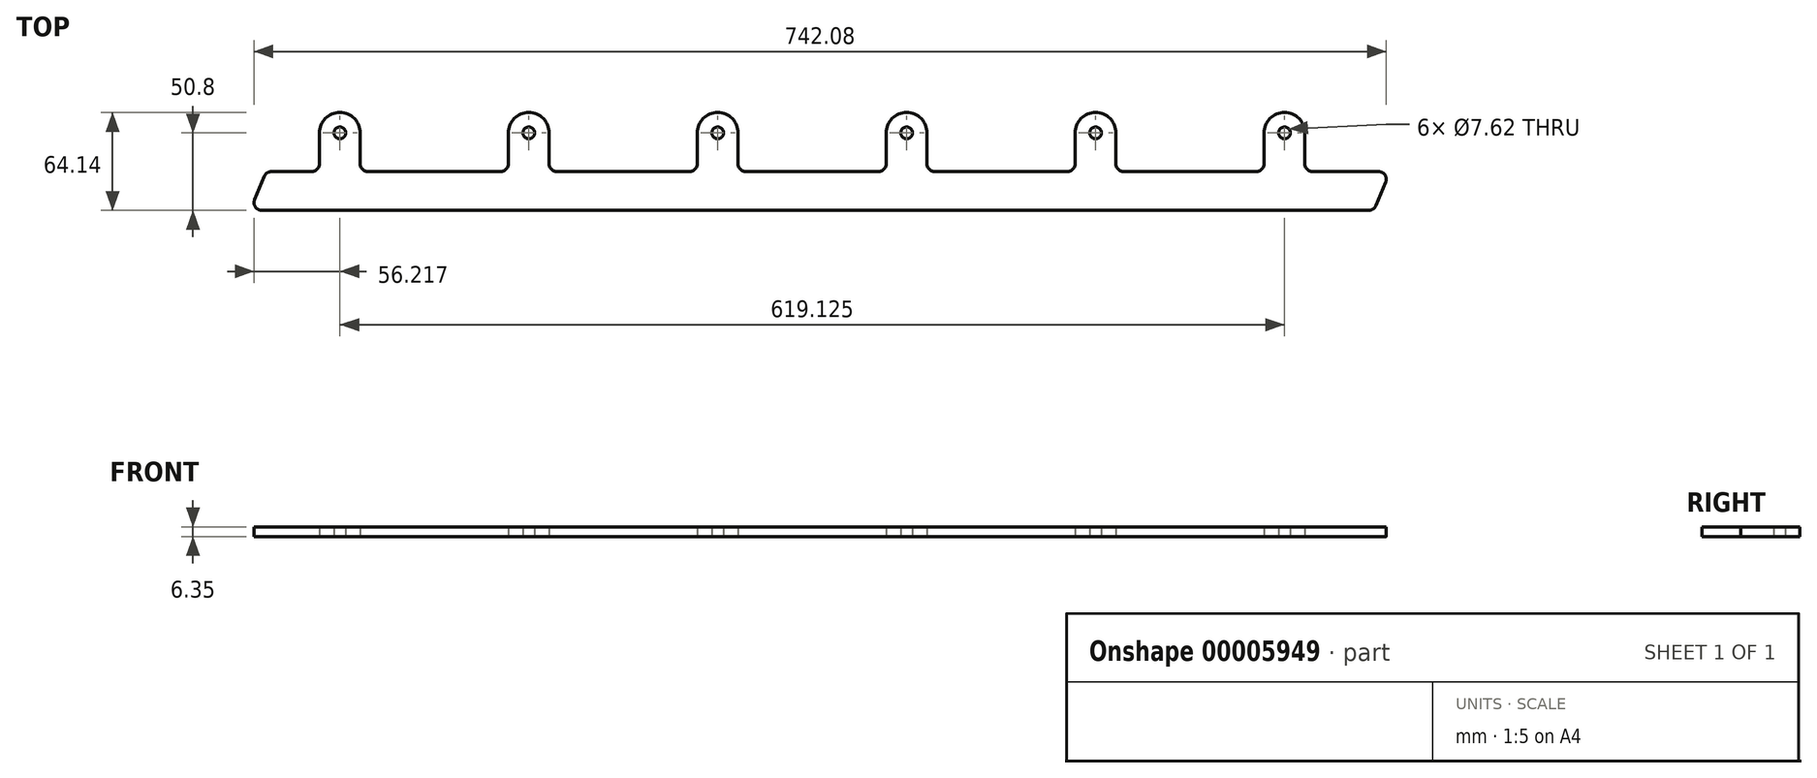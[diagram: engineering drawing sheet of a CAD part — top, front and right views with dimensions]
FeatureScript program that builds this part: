
annotation { "Feature Type Name" : "Feature", "Feature Type Description" : "" }
export const myFeature = defineFeature(function(context is Context, id is Id, definition is map)
    precondition{}
    {
        {
            var Q0;
            Q0=qCreatedBy(makeId("Top.planeOp"),FACE);
            var sketch = newSketch(context, id + "F0", { "sketchPlane" : qUnion([Q0])});
            skLineSegment(sketch, "E0.rect.bottom", {"start": v(368.3, 12.7) * mm, "end": v(-296.23, 12.7) * mm});
            skLineSegment(sketch, "E0.rect.top", {"start": v(368.3, -12.7) * mm, "end": v(-368.3, -12.7) * mm});
            skLineSegment(sketch, "E0.rect.left", {"start": v(368.3, 12.7) * mm, "end": v(368.3, -12.7) * mm, "construction": true});
            skLineSegment(sketch, "E0.rect.right", {"start": v(-368.3, 12.7) * mm, "end": v(-368.3, -12.7) * mm, "construction": true});
            skPoint(sketch, "E0.rect.middle", {"position": v(0, 0) * mm});
            skCircle(sketch, "E1", {"center": v(-309.56, 38.1) * mm, "radius": 3.81 * mm});
            skArc(sketch, "E2.0", {"start": v(-296.23, 38.1) * mm, "mid": v(-309.56, 51.44) * mm, "end": v(-322.9, 38.1) * mm});
            skLineSegment(sketch, "E3", {"start": v(-322.9, 38.1) * mm, "end": v(-322.9, 12.7) * mm});
            skLineSegment(sketch, "E4", {"start": v(-296.23, 38.1) * mm, "end": v(-296.23, 12.7) * mm});
            skLineSegment(sketch, "E5.trimOffspring", {"start": v(-322.9, 12.7) * mm, "end": v(-357.78, 12.7) * mm});
            skLineSegment(sketch, "E6.1.0.0", {"start": v(-199.07, 38.1) * mm, "end": v(-199.07, 12.7) * mm});
            skArc(sketch, "E6.1.0.1", {"start": v(-172.4, 38.1) * mm, "mid": v(-185.74, 51.44) * mm, "end": v(-199.07, 38.1) * mm});
            skCircle(sketch, "E6.1.0.2", {"center": v(-185.74, 38.1) * mm, "radius": 3.81 * mm});
            skLineSegment(sketch, "E6.1.0.3", {"start": v(-172.4, 38.1) * mm, "end": v(-172.4, 12.7) * mm});
            skLineSegment(sketch, "E6.2.0.0", {"start": v(-75.25, 38.1) * mm, "end": v(-75.25, 12.7) * mm});
            skArc(sketch, "E6.2.0.1", {"start": v(-48.58, 38.1) * mm, "mid": v(-61.91, 51.44) * mm, "end": v(-75.25, 38.1) * mm});
            skCircle(sketch, "E6.2.0.2", {"center": v(-61.91, 38.1) * mm, "radius": 3.81 * mm});
            skLineSegment(sketch, "E6.2.0.3", {"start": v(-48.58, 38.1) * mm, "end": v(-48.58, 12.7) * mm});
            skLineSegment(sketch, "E6.3.0.0", {"start": v(48.58, 38.1) * mm, "end": v(48.58, 12.7) * mm});
            skArc(sketch, "E6.3.0.1", {"start": v(75.25, 38.1) * mm, "mid": v(61.91, 51.44) * mm, "end": v(48.58, 38.1) * mm});
            skCircle(sketch, "E6.3.0.2", {"center": v(61.91, 38.1) * mm, "radius": 3.81 * mm});
            skLineSegment(sketch, "E6.3.0.3", {"start": v(75.25, 38.1) * mm, "end": v(75.25, 12.7) * mm});
            skLineSegment(sketch, "E6.4.0.0", {"start": v(172.4, 38.1) * mm, "end": v(172.4, 12.7) * mm});
            skArc(sketch, "E6.4.0.1", {"start": v(199.07, 38.1) * mm, "mid": v(185.74, 51.44) * mm, "end": v(172.4, 38.1) * mm});
            skCircle(sketch, "E6.4.0.2", {"center": v(185.74, 38.1) * mm, "radius": 3.81 * mm});
            skLineSegment(sketch, "E6.4.0.3", {"start": v(199.07, 38.1) * mm, "end": v(199.07, 12.7) * mm});
            skLineSegment(sketch, "E6.direction1", {"start": v(-322.9, 12.7) * mm, "end": v(-199.07, 12.7) * mm, "construction": true});
            skLineSegment(sketch, "E7.0.5.0", {"start": v(296.23, 38.1) * mm, "end": v(296.23, 12.7) * mm});
            skArc(sketch, "E7.3.5.0", {"start": v(322.9, 38.1) * mm, "mid": v(309.56, 51.44) * mm, "end": v(296.23, 38.1) * mm});
            skCircle(sketch, "E7.7.5.0", {"center": v(309.56, 38.1) * mm, "radius": 3.81 * mm});
            skLineSegment(sketch, "E7.9.5.0", {"start": v(322.9, 38.1) * mm, "end": v(322.9, 12.7) * mm});
            skLineSegment(sketch, "E8", {"start": v(48.58, 38.1) * mm, "end": v(-48.58, 38.1) * mm, "construction": true});
            skPoint(sketch, "E9", {"position": v(0, 38.1) * mm});
            skLineSegment(sketch, "E10", {"start": v(-368.3, -12.7) * mm, "end": v(-357.78, 12.7) * mm});
            skLineSegment(sketch, "E11", {"start": v(368.3, -12.7) * mm, "end": v(378.82, 12.7) * mm});
            skLineSegment(sketch, "E12", {"start": v(368.3, 12.7) * mm, "end": v(378.82, 12.7) * mm});
            skSolve(sketch);
        }
        {
            var Q0;
            Q0=makeQuery(id+"F0.imprint","IMPRINT",FACE,{"disambiguationData":[TD([[makeQuery(id+"F0.imprint","IMPRINT",EDGE,{"derivedFrom":sQuery(id+"F0.wireOp",EDGE,"E0.rect.top")}),-1.0]])]});
            var Q1;
            {var subQ1=sQuery(id+"F0.wireOp",EDGE,"E6.1.0.0");Q1=makeQuery(id+"F0.imprint","IMPRINT",FACE,{"disambiguationData":[TD([[makeQuery(id+"F0.imprint","IMPRINT",EDGE,{"derivedFrom":subQ1}),1.0]])]});}
            var Q2;
            {var subQ1=sQuery(id+"F0.wireOp",EDGE,"E6.2.0.0");Q2=makeQuery(id+"F0.imprint","IMPRINT",FACE,{"disambiguationData":[TD([[makeQuery(id+"F0.imprint","IMPRINT",EDGE,{"derivedFrom":subQ1}),1.0]])]});}
            var Q3;
            {var subQ1=sQuery(id+"F0.wireOp",EDGE,"E6.3.0.0");Q3=makeQuery(id+"F0.imprint","IMPRINT",FACE,{"disambiguationData":[TD([[makeQuery(id+"F0.imprint","IMPRINT",EDGE,{"derivedFrom":subQ1}),1.0]])]});}
            var Q4;
            {var subQ1=sQuery(id+"F0.wireOp",EDGE,"E6.4.0.0");Q4=makeQuery(id+"F0.imprint","IMPRINT",FACE,{"disambiguationData":[TD([[makeQuery(id+"F0.imprint","IMPRINT",EDGE,{"derivedFrom":subQ1}),1.0]])]});}
            var Q5;
            {var subQ1=sQuery(id+"F0.wireOp",EDGE,"E7.0.5.0");Q5=makeQuery(id+"F0.imprint","IMPRINT",FACE,{"disambiguationData":[TD([[makeQuery(id+"F0.imprint","IMPRINT",EDGE,{"derivedFrom":subQ1}),1.0]])]});}
            extrude(context, id + "F1", {"entities" : qUnion([Q0, Q1, Q2, Q3, Q4, Q5]), "depth" : 6.35 * mm});
        }
        {
            var Q0;
            Q0=makeQuery(id+"F1.opExtrude","SWEPT_EDGE",EDGE,{"disambiguationData":[OSD([sQuery(id+"F0.wireOp",EDGE,"E0.rect.top"),sQuery(id+"F0.wireOp",EDGE,"E11")])]});
            var Q1;
            Q1=makeQuery(id+"F1.opExtrude","SWEPT_EDGE",EDGE,{"disambiguationData":[OSD([sQuery(id+"F0.wireOp",EDGE,"E0.rect.top"),sQuery(id+"F0.wireOp",EDGE,"E10")])]});
            var Q2;
            Q2=makeQuery(id+"F1.opExtrude","SWEPT_EDGE",EDGE,{"disambiguationData":[OSD([sQuery(id+"F0.wireOp",EDGE,"E3"),sQuery(id+"F0.wireOp",EDGE,"E5.trimOffspring")])]});
            var Q3;
            Q3=makeQuery(id+"F1.opExtrude","SWEPT_EDGE",EDGE,{"disambiguationData":[OSD([sQuery(id+"F0.wireOp",EDGE,"E5.trimOffspring"),sQuery(id+"F0.wireOp",EDGE,"E10")])]});
            var Q4;
            Q4=makeQuery(id+"F1.opExtrude","SWEPT_EDGE",EDGE,{"disambiguationData":[OSD([sQuery(id+"F0.wireOp",EDGE,"E0.rect.bottom"),sQuery(id+"F0.wireOp",EDGE,"E6.1.0.0")])]});
            var Q5;
            Q5=makeQuery(id+"F1.opExtrude","SWEPT_EDGE",EDGE,{"disambiguationData":[OSD([sQuery(id+"F0.wireOp",EDGE,"E0.rect.bottom"),sQuery(id+"F0.wireOp",EDGE,"E6.2.0.0")])]});
            var Q6;
            Q6=makeQuery(id+"F1.opExtrude","SWEPT_EDGE",EDGE,{"disambiguationData":[OSD([sQuery(id+"F0.wireOp",EDGE,"E0.rect.bottom"),sQuery(id+"F0.wireOp",EDGE,"E6.3.0.0")])]});
            var Q7;
            Q7=makeQuery(id+"F1.opExtrude","SWEPT_EDGE",EDGE,{"disambiguationData":[OSD([sQuery(id+"F0.wireOp",EDGE,"E0.rect.bottom"),sQuery(id+"F0.wireOp",EDGE,"E6.4.0.0")])]});
            var Q8;
            Q8=makeQuery(id+"F1.opExtrude","SWEPT_EDGE",EDGE,{"disambiguationData":[OSD([sQuery(id+"F0.wireOp",EDGE,"E0.rect.bottom"),sQuery(id+"F0.wireOp",EDGE,"E7.0.5.0")])]});
            var Q9;
            Q9=makeQuery(id+"F1.opExtrude","SWEPT_EDGE",EDGE,{"disambiguationData":[OSD([sQuery(id+"F0.wireOp",EDGE,"E0.rect.bottom"),sQuery(id+"F0.wireOp",EDGE,"E4")])]});
            var Q10;
            Q10=makeQuery(id+"F1.opExtrude","SWEPT_EDGE",EDGE,{"disambiguationData":[OSD([sQuery(id+"F0.wireOp",EDGE,"E0.rect.bottom"),sQuery(id+"F0.wireOp",EDGE,"E6.1.0.3")])]});
            var Q11;
            Q11=makeQuery(id+"F1.opExtrude","SWEPT_EDGE",EDGE,{"disambiguationData":[OSD([sQuery(id+"F0.wireOp",EDGE,"E0.rect.bottom"),sQuery(id+"F0.wireOp",EDGE,"E6.2.0.3")])]});
            var Q12;
            Q12=makeQuery(id+"F1.opExtrude","SWEPT_EDGE",EDGE,{"disambiguationData":[OSD([sQuery(id+"F0.wireOp",EDGE,"E0.rect.bottom"),sQuery(id+"F0.wireOp",EDGE,"E6.3.0.3")])]});
            var Q13;
            Q13=makeQuery(id+"F1.opExtrude","SWEPT_EDGE",EDGE,{"disambiguationData":[OSD([sQuery(id+"F0.wireOp",EDGE,"E0.rect.bottom"),sQuery(id+"F0.wireOp",EDGE,"E6.4.0.3")])]});
            var Q14;
            Q14=makeQuery(id+"F1.opExtrude","SWEPT_EDGE",EDGE,{"disambiguationData":[OSD([sQuery(id+"F0.wireOp",EDGE,"E0.rect.bottom"),sQuery(id+"F0.wireOp",EDGE,"E7.9.5.0")])]});
            var Q15;
            Q15=makeQuery(id+"F1.opExtrude","SWEPT_EDGE",EDGE,{"disambiguationData":[OSD([sQuery(id+"F0.wireOp",EDGE,"E11"),sQuery(id+"F0.wireOp",EDGE,"E12")])]});
            fillet(context, id + "F2", {"entities" : qUnion([Q0, Q1, Q2, Q3, Q4, Q5, Q6, Q7, Q8, Q9, Q10, Q11, Q12, Q13, Q14, Q15]), "radius" : 5.08 * mm, "tangentPropagation" : true, "allowEdgeOverflow" : false});
        }
    });
